# Revit family: Toilet_Seat-Elongated_Closed_Front-Cleansing-KOHLER-C3-355-K-28229
name_source: partatom
category: Specialty Equipment
units: mm (PartAtom-declared; Revit-internal decimal feet)

## family parameters
Cut with Voids When Loaded = No
Host = Face
OmniClass Number = 23.31.19.19.17
OmniClass Title = Water Closet Seats
Part Type = Normal
Room Calculation Point = No
Round Connector Dimension = Use Diameter
Shared = No

## types (2) — shared parameters
ADA Compliant = No
Apparent Load = 1800 VA
Assembly Code = C1030200
CW Connection = Yes
Cold Water Inlet = Cold Water Inlet
Date Modified = 10/16/2023
Default Elevation = 0"
Description = Bidet Seat
Electrical Connector = Yes
Electrical Note = One Dedicated Circuit Required
HW Connection = No
Height = 5 1/8"
Hot Water Inlet = Hot Water Inlet
Length = 20 5/8"
Manufacturer = Kohler Co.
Master Format 2014 = 22 41 13.13
Master Format 2014 Name = Residential Water Closets
Material = Polypropylene Plastic
Product Documentation Link = https://www.us.kohler.com
Product Name = C3-355
Product Page URL = http://www.us.kohler.com
URL = https://www.us.kohler.com
Vent Connection = No
Voltage = 120 V
Waste Connecton = No
Waste Water Outlet = Waste Water Outlet
WaterSense Certified = No
Width = 15 7/16"

## per-type parameters (varying)
| type | Finish | Model | Type |
| 0-White | Kohler-Plastic-0-White | K-28229-0 | 1 |
| 96-Biscuit | Kohler-Plastic-96-Biscuit | K-28229-96 | 2 |

## geometry (parser evidence)
native form markers: Sweep x6
no freeform markers — native parametric forms only
